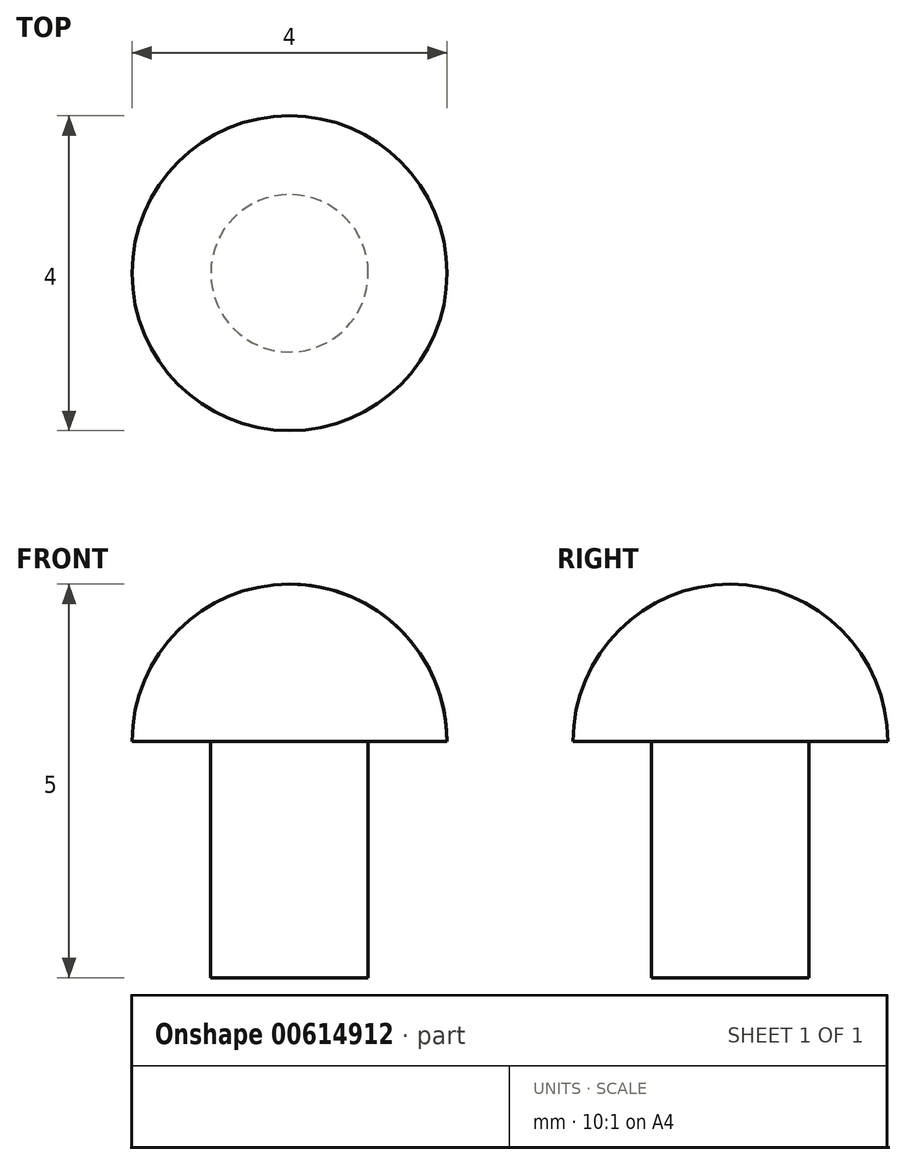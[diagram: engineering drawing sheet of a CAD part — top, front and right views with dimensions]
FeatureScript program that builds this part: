
annotation { "Feature Type Name" : "Feature", "Feature Type Description" : "" }
export const myFeature = defineFeature(function(context is Context, id is Id, definition is map)
    precondition{}
    {
        {
            var Q0;
            Q0=qCreatedBy(makeId("Front.planeOp"),FACE);
            var sketch = newSketch(context, id + "F0", { "sketchPlane" : qUnion([Q0])});
            skArc(sketch, "E0", {"start": v(2, 0) * mm, "mid": v(1.41, 1.41) * mm, "end": v(0, 2) * mm});
            skLineSegment(sketch, "E1", {"start": v(0, 2) * mm, "end": v(0, 0) * mm});
            skLineSegment(sketch, "E2", {"start": v(2, 0) * mm, "end": v(0, 0) * mm});
            skSolve(sketch);
        }
        {
            var Q0;
            Q0 = qSketchRegion(id + "F0", true);
            var Q1;
            Q1=sQuery(id+"F0.wireOp",EDGE,"E1");
            revolve(context, id + "F1", {"entities" : qUnion([Q0]), "axis" : qUnion([Q1]), "revolveType" : RevolveType.FULL});
        }
        {
            var Q0;
            Q0=makeQuery(id+"F1.opRevolve","SWEPT_FACE",FACE,{"disambiguationData":[OSD([sQuery(id+"F0.wireOp",EDGE,"E2")])]});
            var sketch = newSketch(context, id + "F2", { "sketchPlane" : qUnion([Q0])});
            skCircle(sketch, "E3", {"center": v(0, 0) * mm, "radius": 1 * mm});
            skSolve(sketch);
        }
        {
            var Q0;
            Q0=makeQuery(id+"F2.imprint","IMPRINT",FACE,{"disambiguationData":[TD([[makeQuery(id+"F2.imprint","IMPRINT",EDGE,{"derivedFrom":sQuery(id+"F2.wireOp",EDGE,"E3")}),1.0]])]});
            extrude(context, id + "F3", {"entities" : qUnion([Q0]), "operationType" : NewBodyOperationType.ADD, "depth" : 3 * mm, "offsetDistance" : 25 * mm});
        }
    });
